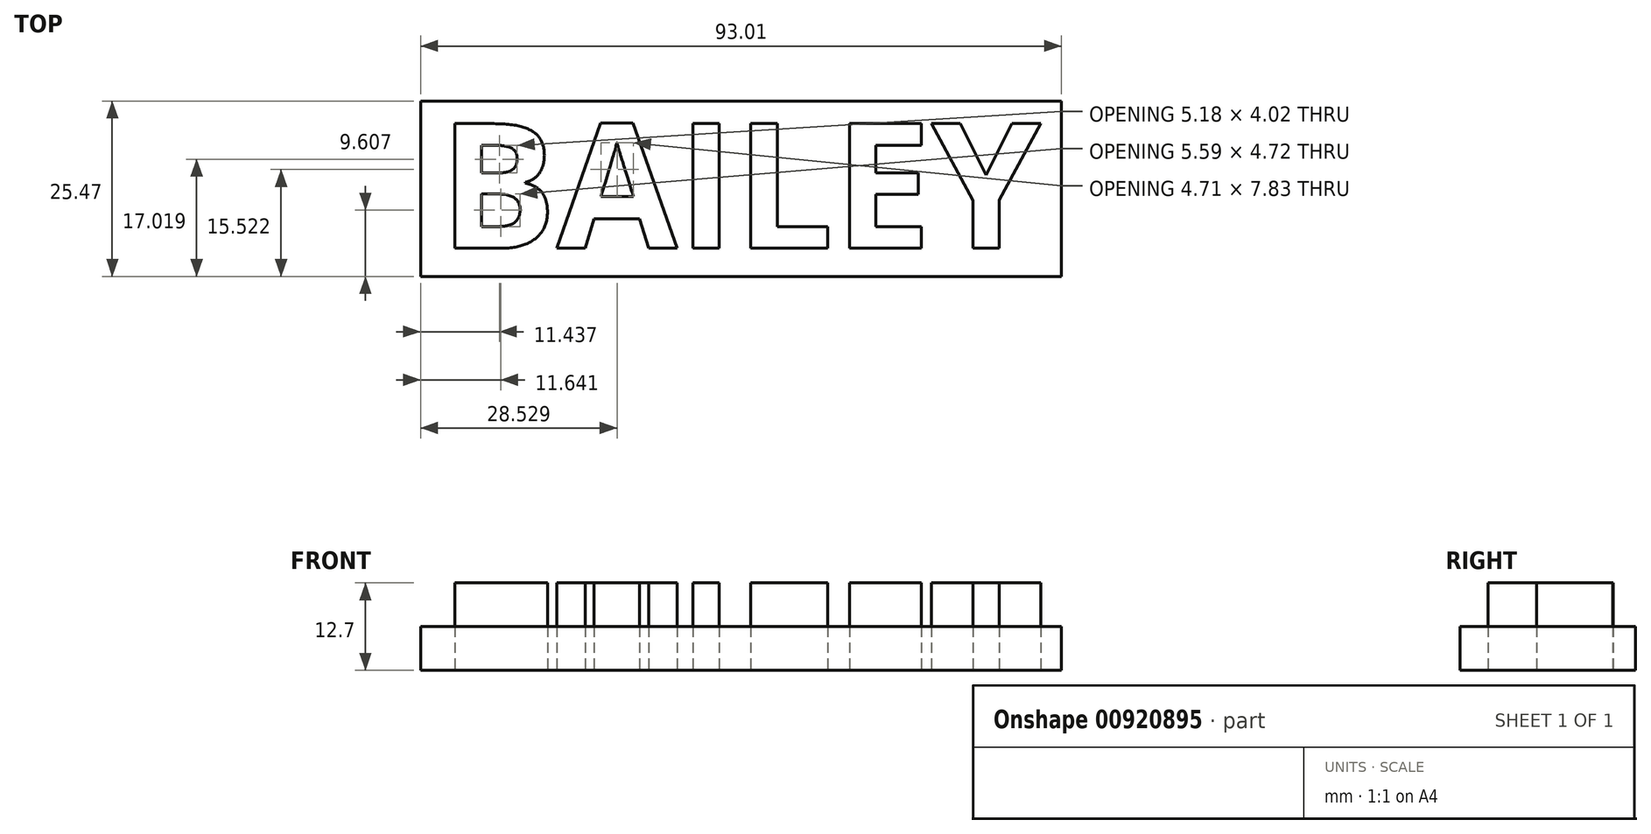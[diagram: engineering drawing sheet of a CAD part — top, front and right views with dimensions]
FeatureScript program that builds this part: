
annotation { "Feature Type Name" : "Feature", "Feature Type Description" : "" }
export const myFeature = defineFeature(function(context is Context, id is Id, definition is map)
    precondition{}
    {
        {
            var Q0;
            Q0=qCreatedBy(makeId("Top.planeOp"),FACE);
            var sketch = newSketch(context, id + "F0", { "sketchPlane" : qUnion([Q0])});
            skText(sketch, "E0", { "text": "BAILEY", "fontName": "OpenSans-Bold.ttf"});
            const initialGuessF0  = {"E0": [-0.04498, -0.00964, 1, 0, 0.01825]};
            skSetInitialGuess(sketch, initialGuessF0);
            skSolve(sketch);
        }
        {
            var Q0;
            Q0 = qSketchRegion(id + "F0", true);
            extrude(context, id + "F1", {"entities" : qUnion([Q0]), "depth" : 12.7 * mm, "offsetDistance" : 25.4 * mm});
        }
        {
            var Q0;
            Q0=qCreatedBy(makeId("Top.planeOp"),FACE);
            var sketch = newSketch(context, id + "F2", { "sketchPlane" : qUnion([Q0])});
            skLineSegment(sketch, "E1.bottom", {"start": v(-47.71, 11.75) * mm, "end": v(45.3, 11.75) * mm});
            skLineSegment(sketch, "E1.top", {"start": v(-47.71, -13.72) * mm, "end": v(45.3, -13.72) * mm});
            skLineSegment(sketch, "E1.left", {"start": v(-47.71, 11.75) * mm, "end": v(-47.71, -13.72) * mm});
            skLineSegment(sketch, "E1.right", {"start": v(45.3, 11.75) * mm, "end": v(45.3, -13.72) * mm});
            skSolve(sketch);
        }
        {
            var Q0;
            Q0=makeQuery(id+"F2.imprint","IMPRINT",FACE,{"disambiguationData":[TD([[makeQuery(id+"F2.imprint","IMPRINT",EDGE,{"derivedFrom":sQuery(id+"F2.wireOp",EDGE,"E1.bottom")}),-1.0]])]});
            extrude(context, id + "F3", {"entities" : qUnion([Q0]), "depth" : 6.35 * mm, "offsetDistance" : 25.4 * mm});
        }
    });
